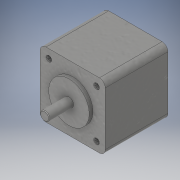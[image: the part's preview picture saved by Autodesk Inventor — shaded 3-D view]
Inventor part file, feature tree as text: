
AUTODESK INVENTOR PART (.ipt)
format: ipt  version: 2017 (Build 210142000, 142)  size: 637,952 bytes
history: native  units: in
note: dims shown in document units (in); Inventor stores cm internally (conversion verified against a paired STEP export)
features: chamfer x1, other x1
ambient origin geometry x8: Origin, YZ Plane, XZ Plane, XY Plane, X Axis, Y Axis, Z Axis, Center Point
bodies: Solid1 (feature_tree), Solid2 (feature_tree)
feature tree (2):
  chamfer  "Chamfer1"  [1 undecoded]
  other  "LPattern1"
note: 1 required parameter value undecoded (feature->parameter linkage not recoverable at this tier; creation-order binding heuristic only, values carry confidence <= 0.55)
